# Revit family: Fireclass_Addressable Base Sounder_Visual Alarm Devices
name_source: partatom
category: Fire Alarm Devices
revit_build: Autodesk Revit 2014 (Build: 20130308_1515(x64)
units: mm (PartAtom-declared; Revit-internal decimal feet)

## types (2) — shared parameters
Asset Type = Moveable
Brand = FireClass
Category = Pr_70_75_02_97
Colour = Transluscent
Duration Unit = Year
Finish = TBC
Has Protective Earth = No
Ifc Export As = TBC
Ifc Export Type = TBC
Ifc Type Object = IfcBuildingElementProxy
Installation Date = TBC
LED = Yes
Manufacturer = Tyco Fire Protection Products
Manufacturer Name = Tyco Fire Protection Products
Manufacturer URL = www.fireclass.co.uk
Material = TBC
NBS Description = Visual Alarm Signal Devices
NBS Reference = 90-75-30/415
Nominal  Diameter = 135.0 mm
Nominal Current = 1.1A
Nominal Height = 45.0 mm
Nominal Length = 135.0 mm
Nominal Voltage = 40 V DC
Nominal Width = 135.0 mm
Operation Temperature Range = -25 to +70
Product Information = TBC
Quiescent Current = 400uA
Relative Humidity = Up to 95% non-condensing
Shape = Circular
Short Circuit Isolators = Yes
Storage Temperature = -25 to +70
URL = TBC
Uniclass2 = Pr_70_75_02_97
Version = 1
Voltage = 20V-40V, 35V nominal
Warranty Duration Labor = 3 years
Warranty Duration Parts = 3 years (TBC)
Warranty Duration Unit = Year
Warranty Start Date = TBC
Weight = 187g

## per-type parameters (varying)
| type | Alarm Current | BIM Object Name | Description | Electrical Device Nominal Power | Features | Model | Model Reference | Name | Product Codes | Product Specification |
| Fireclass Addressable Base Sounder-Beacon VAD Standard Power | 14mA | Tyco_FireDtctnAlmCtrlIndctEquip_FireClass-AddressableBaseSounderBeaconVADStandardPower-FC440AVB | FC440AVB FireClass Addressable Base Sounder Beacon Visual Alarm Device White LEDs Standard Power | 490mW | Addressable Base Sounder-Beacon VAD Standard Power | FC440AVB | FC440AVB FireClass Addressable Base Sounder Beacon VAD Standard Power | FC440AVB Add Sdr Base VAD Std | 576.440.006 | FC440AVB FireClass Addressable Base Sounder Beacon VAD Standard Power |
| Fireclass Addressable Base Sounder-Beacon VAD High Power | 31mA | Tyco_FireDtct_FireClass-AddressableBaseSounderBeaconVADHighPower-FC441AVB | FC441AVB FireClass Addressable Base Sounder Beacon Visual Alarm Device White LEDs High Power | 1.1W | Addressable Base Sounder-Beacon VAD High Power | FC441AVB | FC441AVB FireClass Addressable Base Sounder Beacon VAD High Power | FC441AVB Add Sdr Base VAD High | 576.080.014 | FC441AVB Zettler Addressable Base Sounder Beacon VAD High Power |

## geometry (parser evidence)
native form markers: Sweep x4
no freeform markers — native parametric forms only
